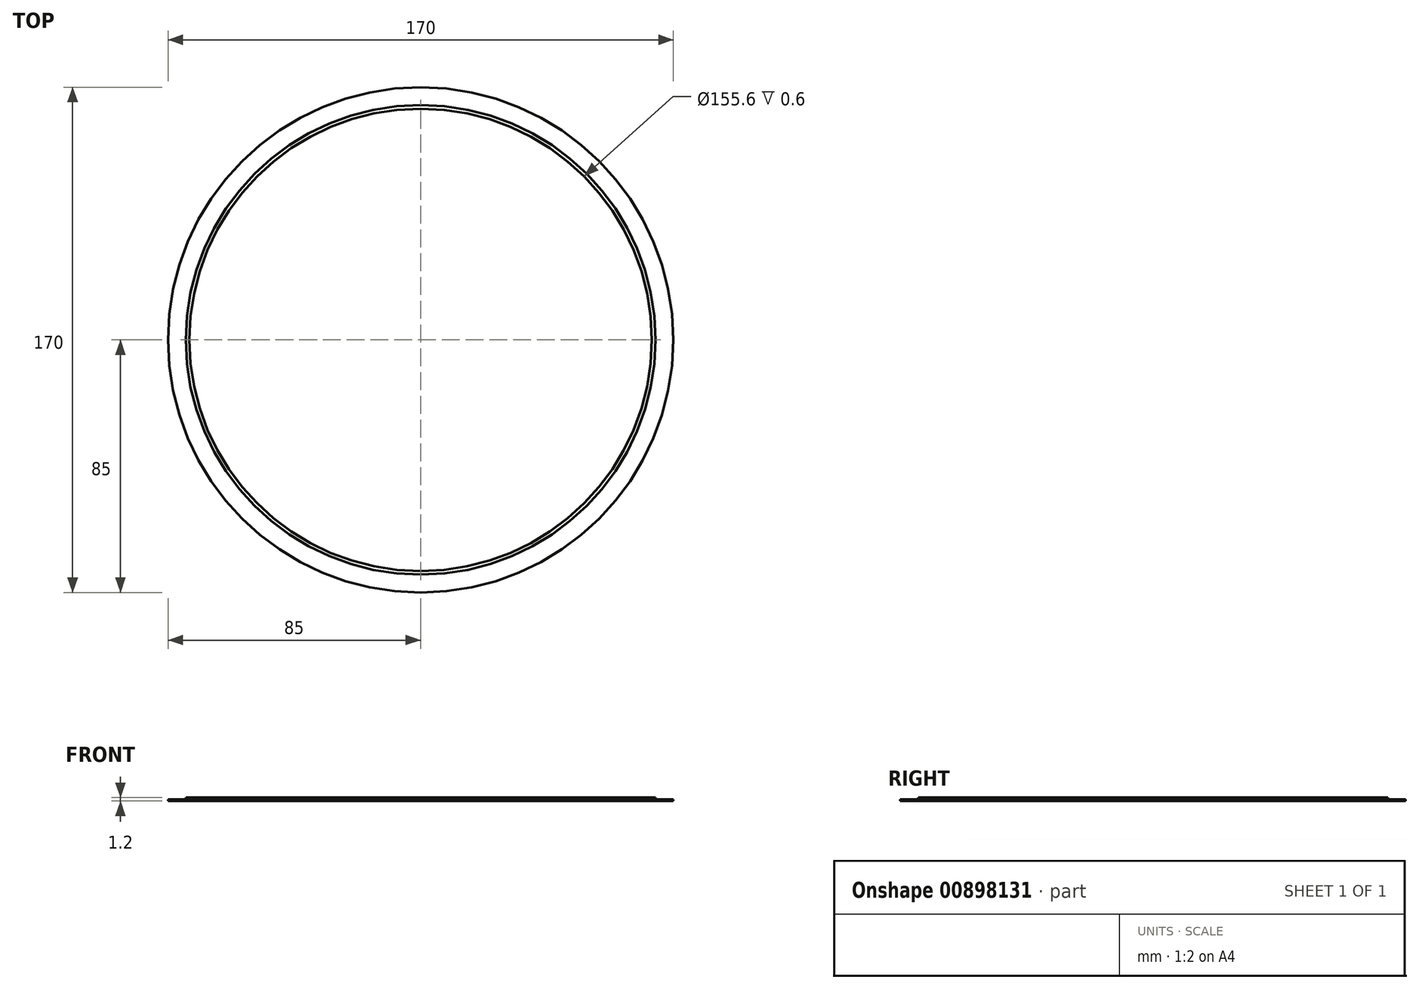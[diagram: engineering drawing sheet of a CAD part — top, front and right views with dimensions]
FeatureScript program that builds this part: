
annotation { "Feature Type Name" : "Feature", "Feature Type Description" : "" }
export const myFeature = defineFeature(function(context is Context, id is Id, definition is map)
    precondition{}
    {
        {
            var Q0;
            Q0=qCreatedBy(makeId("Top.planeOp"),FACE);
            var sketch = newSketch(context, id + "F0", { "sketchPlane" : qUnion([Q0])});
            skCircle(sketch, "E0", {"center": v(0, 0) * mm, "radius": 85 * mm});
            skCircle(sketch, "E1", {"center": v(0, 0) * mm, "radius": 79 * mm});
            skCircle(sketch, "E2", {"center": v(0, 0) * mm, "radius": 77.8 * mm});
            skSolve(sketch);
        }
        {
            var Q0;
            Q0=makeQuery(id+"F0.imprint","IMPRINT",FACE,{"disambiguationData":[TD([[makeQuery(id+"F0.imprint","IMPRINT",EDGE,{"derivedFrom":sQuery(id+"F0.wireOp",EDGE,"E1")}),1.0]])]});
            extrude(context, id + "F1", {"entities" : qUnion([Q0]), "depth" : 0.6 * mm, "offsetDistance" : 25 * mm});
        }
        {
            var Q0;
            Q0=makeQuery(id+"F0.imprint","IMPRINT",FACE,{"disambiguationData":[TD([[makeQuery(id+"F0.imprint","IMPRINT",EDGE,{"derivedFrom":sQuery(id+"F0.wireOp",EDGE,"E2")}),1.0]])]});
            var Q1;
            Q1=makeQuery(id+"F0.imprint","IMPRINT",FACE,{"disambiguationData":[TD([[makeQuery(id+"F0.imprint","IMPRINT",EDGE,{"derivedFrom":sQuery(id+"F0.wireOp",EDGE,"E1")}),1.0]])]});
            var Q2;
            Q2=makeQuery(id+"F0.imprint","IMPRINT",FACE,{"disambiguationData":[TD([[makeQuery(id+"F0.imprint","IMPRINT",EDGE,{"derivedFrom":sQuery(id+"F0.wireOp",EDGE,"E0")}),1.0]])]});
            extrude(context, id + "F2", {"entities" : qUnion([Q0, Q1, Q2]), "operationType" : NewBodyOperationType.ADD, "oppositeDirection" : true, "depth" : 0.6 * mm, "offsetDistance" : 25 * mm});
        }
    });
